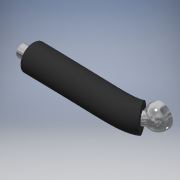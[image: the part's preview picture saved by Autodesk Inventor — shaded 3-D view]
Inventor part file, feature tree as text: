
AUTODESK INVENTOR PART (.ipt)
format: ipt  version: 2019.4 (Build 234330000, 330)  size: 230,912 bytes
history: native  units: mm
features: sketch x5, sweep x2, extrude x1, fillet x1, plane x1
ambient origin geometry x8: Origin, YZ Plane, XZ Plane, XY Plane, X Axis, Y Axis, Z Axis, Center Point
bodies: Solid1 (feature_tree)
feature tree (10):
  extrude  "Extrusion1"  Depth=2.5mm TaperAngle=0.0deg
  fillet  "Fillet1"  Radius=2.0mm
  sweep  "Sweep1"
  plane  "Work Plane1"
  sweep  "Sweep3"
  sketch  "Sketch1"  dims[d0=4.0mm d1=2.5mm d2=0.0mm d3=2.0mm]
  sketch  "Sketch2"  dims[d4=2.5mm d5=2.053mm]
  sketch  "Sketch3"  dims[d6=0.0mm d7=0.0mm d8=-2.0mm]
  sketch  "Sketch4"  dims[d9=4.5mm]
  sketch  "Sketch5"  dims[d10=4.712389mm d11=1.5mm d12=4.0mm d16=0.0mm d17=0.0mm]
